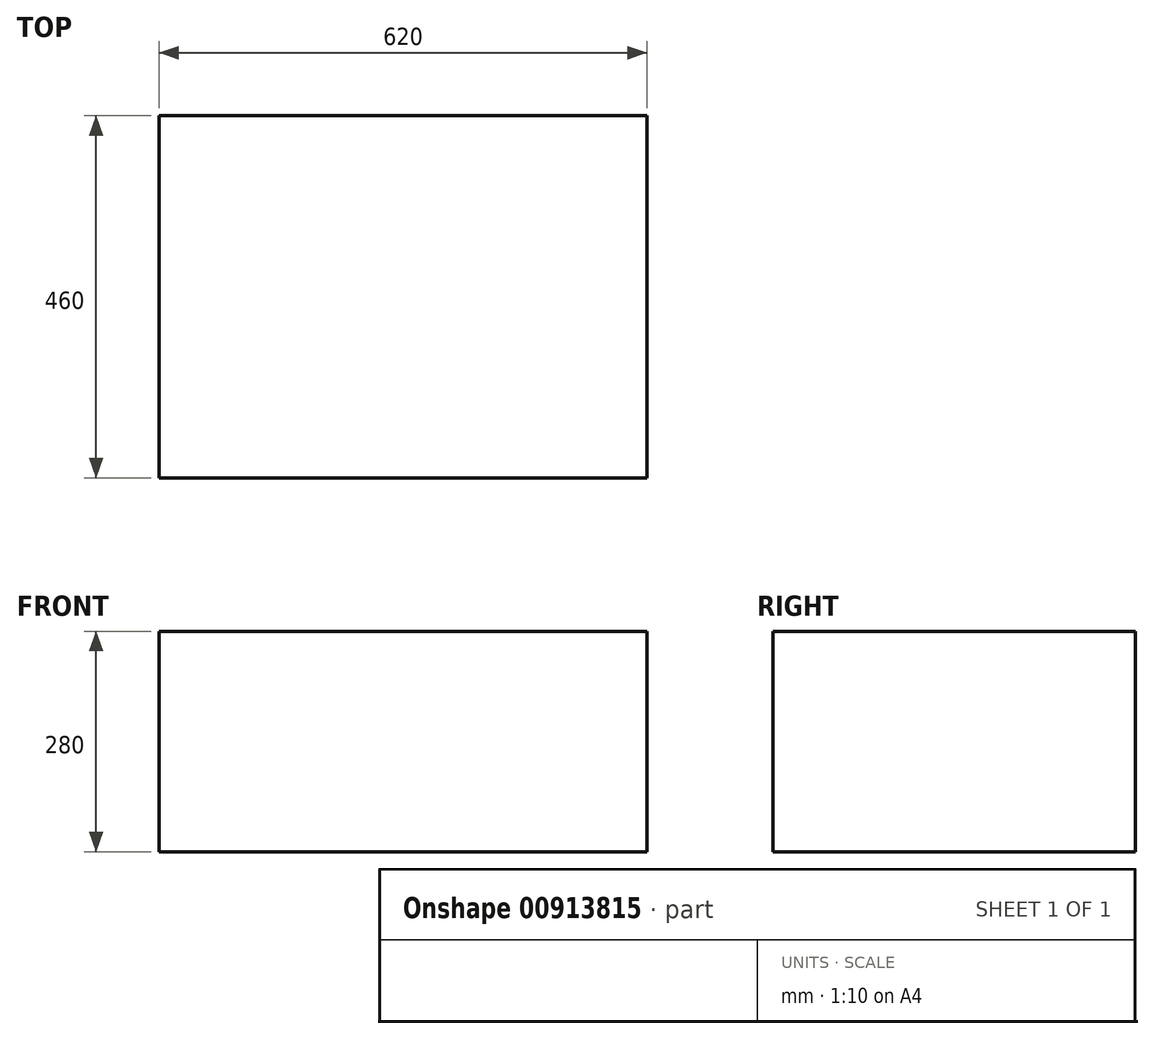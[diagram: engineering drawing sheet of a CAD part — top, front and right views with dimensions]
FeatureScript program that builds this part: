
annotation { "Feature Type Name" : "Feature", "Feature Type Description" : "" }
export const myFeature = defineFeature(function(context is Context, id is Id, definition is map)
    precondition{}
    {
        {
            var Q0;
            Q0=qCreatedBy(makeId("Top.planeOp"),FACE);
            var sketch = newSketch(context, id + "F0", { "sketchPlane" : qUnion([Q0])});
            skLineSegment(sketch, "E0.bottom", {"start": v(310, -230) * mm, "end": v(-310, -230) * mm});
            skLineSegment(sketch, "E0.top", {"start": v(310, 230) * mm, "end": v(-310, 230) * mm});
            skLineSegment(sketch, "E0.left", {"start": v(310, -230) * mm, "end": v(310, 230) * mm});
            skLineSegment(sketch, "E0.right", {"start": v(-310, -230) * mm, "end": v(-310, 230) * mm});
            skLineSegment(sketch, "E1.bottom", {"start": v(320, -240) * mm, "end": v(-320, -240) * mm});
            skLineSegment(sketch, "E1.top", {"start": v(320, 240) * mm, "end": v(-320, 240) * mm});
            skLineSegment(sketch, "E1.left", {"start": v(320, -240) * mm, "end": v(320, 240) * mm});
            skLineSegment(sketch, "E1.right", {"start": v(-320, -240) * mm, "end": v(-320, 240) * mm});
            skLineSegment(sketch, "E2.bottom", {"start": v(240, -180) * mm, "end": v(-240, -180) * mm});
            skLineSegment(sketch, "E2.top", {"start": v(240, -135) * mm, "end": v(-240, -135) * mm});
            skLineSegment(sketch, "E2.left", {"start": v(240, -180) * mm, "end": v(240, -135) * mm});
            skLineSegment(sketch, "E2.right", {"start": v(-240, -180) * mm, "end": v(-240, -135) * mm});
            skPoint(sketch, "E2.middle", {"position": v(0, 0) * mm});
            skLineSegment(sketch, "E3.0.1.0", {"start": v(240, -85) * mm, "end": v(240, -40) * mm});
            skLineSegment(sketch, "E3.0.1.1", {"start": v(240, -85) * mm, "end": v(-240, -85) * mm});
            skLineSegment(sketch, "E3.0.1.2", {"start": v(240, -40) * mm, "end": v(-240, -40) * mm});
            skLineSegment(sketch, "E3.0.1.3", {"start": v(-240, -85) * mm, "end": v(-240, -40) * mm});
            skLineSegment(sketch, "E3.0.2.0", {"start": v(240, 10) * mm, "end": v(240, 55) * mm});
            skLineSegment(sketch, "E3.0.2.1", {"start": v(240, 10) * mm, "end": v(-240, 10) * mm});
            skLineSegment(sketch, "E3.0.2.2", {"start": v(240, 55) * mm, "end": v(-240, 55) * mm});
            skLineSegment(sketch, "E3.0.2.3", {"start": v(-240, 10) * mm, "end": v(-240, 55) * mm});
            skLineSegment(sketch, "E3.direction1", {"start": v(-240, -180) * mm, "end": v(-215, -180) * mm, "construction": true});
            skLineSegment(sketch, "E3.direction2", {"start": v(-240, -180) * mm, "end": v(-240, -85) * mm, "construction": true});
            skSolve(sketch);
        }
        {
            var Q0;
            Q0=makeQuery(id+"F0.imprint","IMPRINT",FACE,{"disambiguationData":[TD([[makeQuery(id+"F0.imprint","IMPRINT",EDGE,{"derivedFrom":sQuery(id+"F0.wireOp",EDGE,"E0.bottom")}),-1.0]])]});
            var Q1;
            Q1=makeQuery(id+"F0.imprint","IMPRINT",FACE,{"disambiguationData":[TD([[makeQuery(id+"F0.imprint","IMPRINT",EDGE,{"derivedFrom":sQuery(id+"F0.wireOp",EDGE,"E3.0.2.0")}),1.0]])]});
            var Q2;
            Q2=makeQuery(id+"F0.imprint","IMPRINT",FACE,{"disambiguationData":[TD([[makeQuery(id+"F0.imprint","IMPRINT",EDGE,{"derivedFrom":sQuery(id+"F0.wireOp",EDGE,"E3.0.1.0")}),1.0]])]});
            var Q3;
            Q3=makeQuery(id+"F0.imprint","IMPRINT",FACE,{"disambiguationData":[TD([[makeQuery(id+"F0.imprint","IMPRINT",EDGE,{"derivedFrom":sQuery(id+"F0.wireOp",EDGE,"E2.bottom")}),-1.0]])]});
            extrude(context, id + "F1", {"entities" : qUnion([Q0, Q1, Q2, Q3]), "oppositeDirection" : true, "depth" : 280 * mm, "offsetDistance" : 25 * mm});
        }
    });
